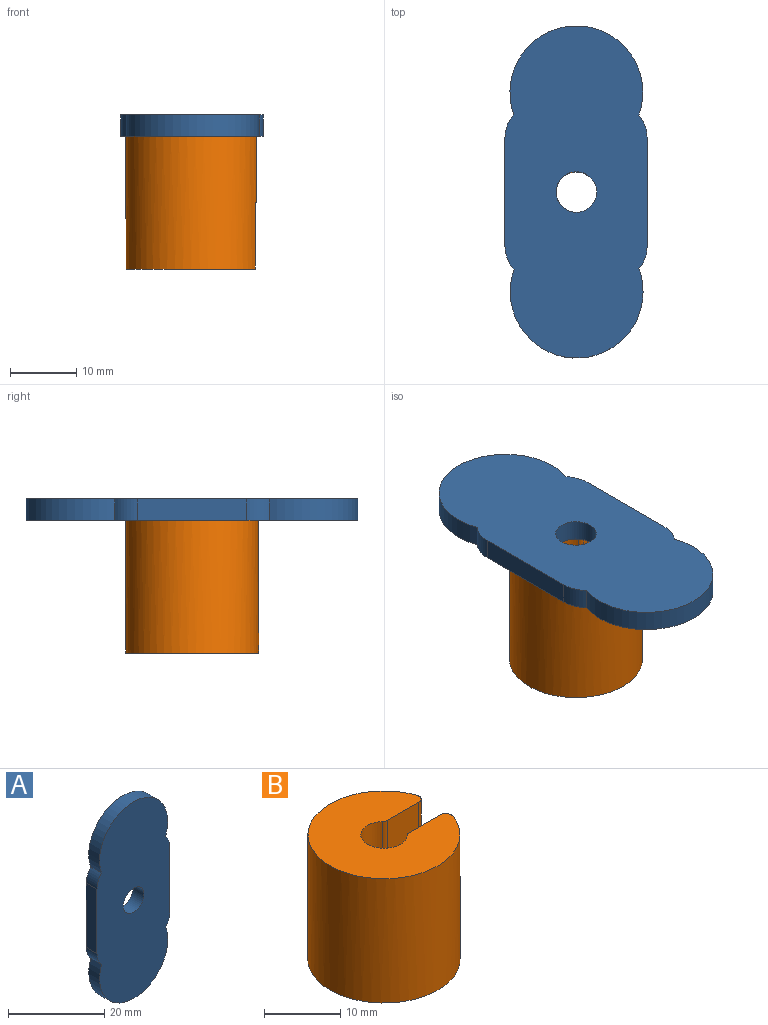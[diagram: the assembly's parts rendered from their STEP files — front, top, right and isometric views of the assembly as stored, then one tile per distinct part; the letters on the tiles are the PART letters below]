
ASSEMBLY  parts=2 mates=1
PART A: 11 faces, bbox 21.4x3.2x50 mm
  f0: cylinder r=5mm len=3.43mm, axis (0,1,0), area 12mm2, adj f1,f7,f9,f10
  f1: cylinder r=10mm len=20mm, axis (0,1,0), area 121.8mm2, adj f0,f2,f9,f10
  f2: cylinder r=5mm len=3.26mm, axis (0,1,0), area 11.3mm2, adj f1,f3,f9,f10
  f3: plane 16.53x3.18mm, normal (1,0,0), area 52.5mm2, adj f2,f4,f9,f10
  f4: cylinder r=5mm len=3.3mm, axis (0,1,0), area 11.4mm2, adj f3,f5,f9,f10
  f5: cylinder r=10mm len=20mm, axis (0,1,0), area 121.9mm2, adj f4,f6,f9,f10
  f6: cylinder r=5mm len=3.41mm, axis (0,1,0), area 11.9mm2, adj f5,f7,f9,f10
  f7: plane 16.37x3.18mm, normal (-1,0,0), area 52mm2, adj f0,f6,f9,f10
  f8: cylinder r=3.05mm len=6.1mm, axis (0,1,0), area 60.8mm2, adj f9,f10
  f9: plane 49.98x21.38mm, normal (0,-1,0), area 908.3mm2, adj f0,f1,f2,f3,f4,f5,f6,f7
  f10: plane 49.98x21.38mm, normal (0,1,0), area 908.3mm2, adj f0,f1,f2,f3,f4,f5,f6,f7
PART B: 18 faces, bbox 19.6x20x20 mm
  f0: cylinder r=3.05mm len=20mm, axis (0,0,-1), area 291.8mm2, adj f4,f5,f6,f9,f11,f12,f14,f17
  f1: plane 10x5.76mm, normal (0,-1,0), area 57.6mm2, adj f4,f6,f7,f12
  f2: cylinder r=10mm len=20mm, axis (0,0,-1), area 1132.4mm2, adj f4,f5,f7,f8,f11,f12,f15,f16
  f3: plane 10x5.76mm, normal (0,1,0), area 57.6mm2, adj f4,f8,f9,f11
  f4: plane 20x19.49mm, normal (0,0,1), area 255.6mm2, adj f0,f1,f2,f3,f6,f7,f8,f9
  f5: plane 20x19.65mm, normal (0,0,-1), area 263mm2, adj f0,f2,f10,f13,f14,f15,f16,f17
  f6: cylinder r=1mm len=10mm, axis (0,0,-1), area 7.4mm2, adj f0,f1,f4,f12
  f7: cylinder r=1mm len=10mm, axis (0,0,-1), area 19.1mm2, adj f1,f2,f4,f12
  f8: cylinder r=1mm len=10mm, axis (0,0,-1), area 19.1mm2, adj f2,f3,f4,f11
  f9: cylinder r=1mm len=10mm, axis (0,0,-1), area 7.4mm2, adj f0,f3,f4,f11
  f10: plane 10x5.46mm, normal (0,1,0), area 54.6mm2, adj f5,f11,f16,f17
  f11: plane 7.6x1.83mm, normal (0,0,1), area 3.7mm2, adj f0,f2,f3,f8,f9,f10,f16,f17
  f12: plane 7.6x1.83mm, normal (0,0,1), area 3.7mm2, adj f0,f1,f2,f6,f7,f13,f14,f15
  f13: plane 10x5.46mm, normal (0,-1,0), area 54.6mm2, adj f5,f12,f14,f15
  f14: cylinder r=1mm len=10mm, axis (0,0,-1), area 9.1mm2, adj f0,f5,f12,f13
  f15: cylinder r=1mm len=10mm, axis (0,0,-1), area 18.5mm2, adj f2,f5,f12,f13
  f16: cylinder r=1mm len=10mm, axis (0,0,-1), area 18.5mm2, adj f2,f5,f10,f11
  f17: cylinder r=1mm len=10mm, axis (0,0,-1), area 9.1mm2, adj f0,f5,f10,f11
PLACE A rot(axis=(-1,0,0),90deg) t=(-4.39,5.31,15.95)mm
PLACE B rot(axis=(1,0,0),180deg) t=(-4.39,5.31,15.95)mm
MATE fastened B.f0 <-> A.f8  axis (0,0,1) through (-4.39,5.31,15.95)mm
